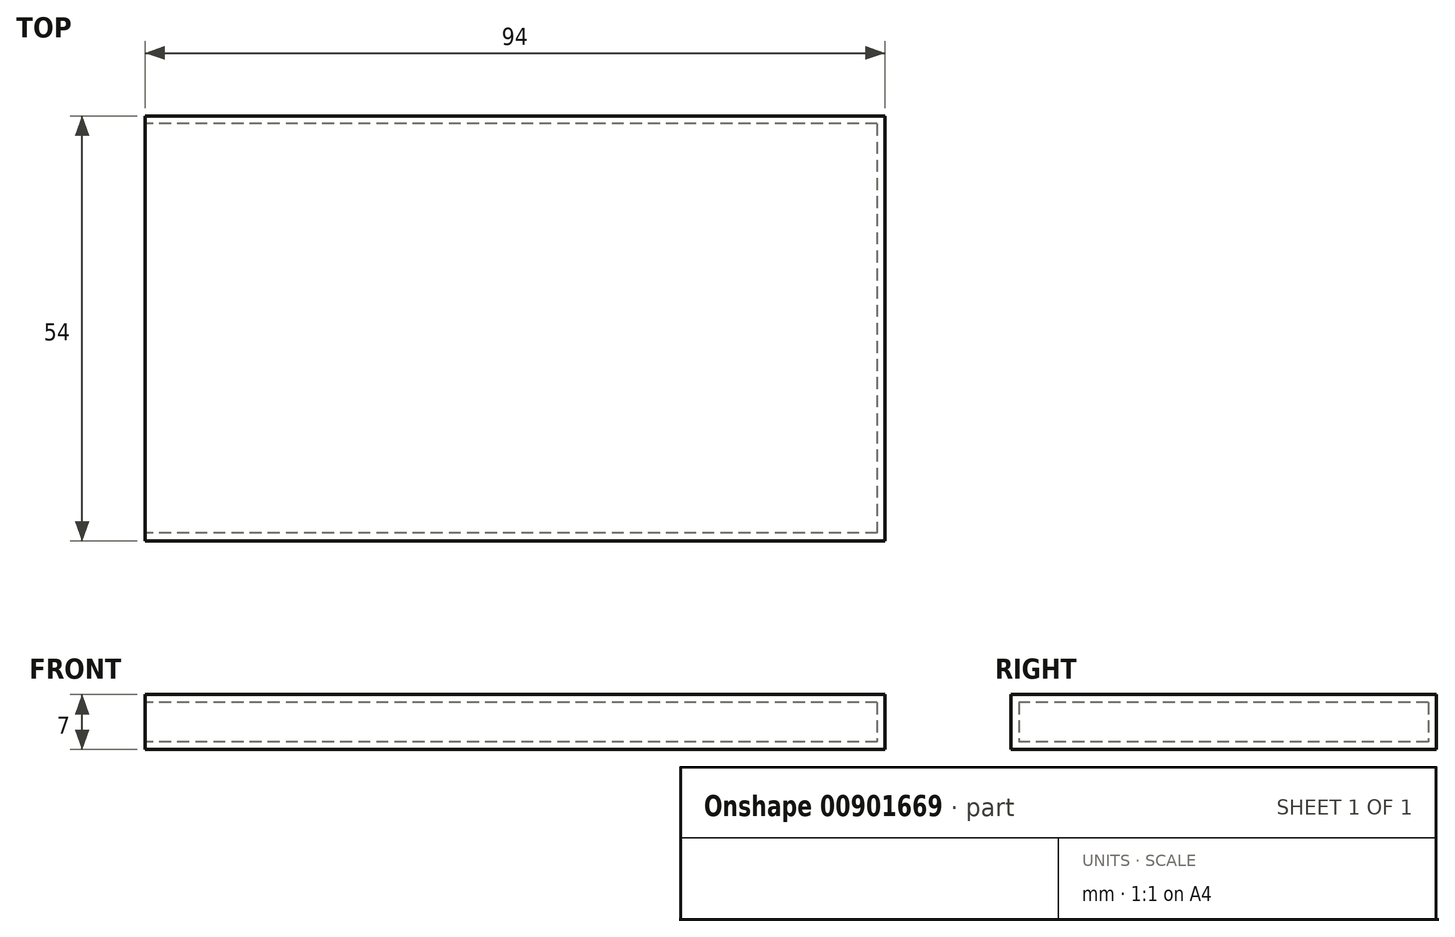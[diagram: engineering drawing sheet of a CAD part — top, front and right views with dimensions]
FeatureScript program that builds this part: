
annotation { "Feature Type Name" : "Feature", "Feature Type Description" : "" }
export const myFeature = defineFeature(function(context is Context, id is Id, definition is map)
    precondition{}
    {
        {
            assignVariable(context, id + "F0", {"name" : "CardDepth", "anyValue" : 3 * mm});
        }
        {
            var Q0;
            Q0=qCreatedBy(makeId("Top.planeOp"),FACE);
            var sketch = newSketch(context, id + "F1", { "sketchPlane" : qUnion([Q0])});
            skLineSegment(sketch, "E0.bottom", {"start": v(47, 27) * mm, "end": v(-47, 27) * mm});
            skLineSegment(sketch, "E0.top", {"start": v(47, -27) * mm, "end": v(-47, -27) * mm});
            skLineSegment(sketch, "E0.left", {"start": v(47, 27) * mm, "end": v(47, -27) * mm});
            skLineSegment(sketch, "E0.right", {"start": v(-47, 27) * mm, "end": v(-47, -27) * mm});
            skPoint(sketch, "E0.middle", {"position": v(0, 0) * mm});
            skSolve(sketch);
        }
        {
            var Q0;
            Q0 = qSketchRegion(id + "F1", true);
            extrude(context, id + "F2", {"entities" : qUnion([Q0]), "depth" : getVariable(context, 'CardDepth') + 4 * mm, "offsetDistance" : 25 * mm});
        }
        {
            var Q0;
            Q0=makeQuery(id+"F2.opExtrude","SWEPT_FACE",FACE,{"disambiguationData":[OSD([sQuery(id+"F1.wireOp",EDGE,"E0.right")])]});
            var sketch = newSketch(context, id + "F3", { "sketchPlane" : qUnion([Q0])});
            skLineSegment(sketch, "E1.bottom", {"start": v(-26, 6) * mm, "end": v(26, 6) * mm});
            skLineSegment(sketch, "E1.top", {"start": v(-26, 1) * mm, "end": v(26, 1) * mm});
            skLineSegment(sketch, "E1.left", {"start": v(-26, 6) * mm, "end": v(-26, 1) * mm});
            skLineSegment(sketch, "E1.right", {"start": v(26, 6) * mm, "end": v(26, 1) * mm});
            skSolve(sketch);
        }
        {
            var Q0;
            Q0 = qSketchRegion(id + "F3", true);
            var Q1;
            Q1=makeQuery(id+"F2.opExtrude","SWEPT_FACE",FACE,{"disambiguationData":[OSD([sQuery(id+"F1.wireOp",EDGE,"E0.left")])]});
            extrude(context, id + "F4", {"entities" : qUnion([Q0]), "operationType" : NewBodyOperationType.REMOVE, "endBound" : BoundingType.UP_TO_SURFACE, "oppositeDirection" : true, "depth" : 25 * mm, "endBoundEntityFace" : qUnion([Q1]), "hasOffset" : true, "offsetDistance" : 1 * mm});
        }
    });
